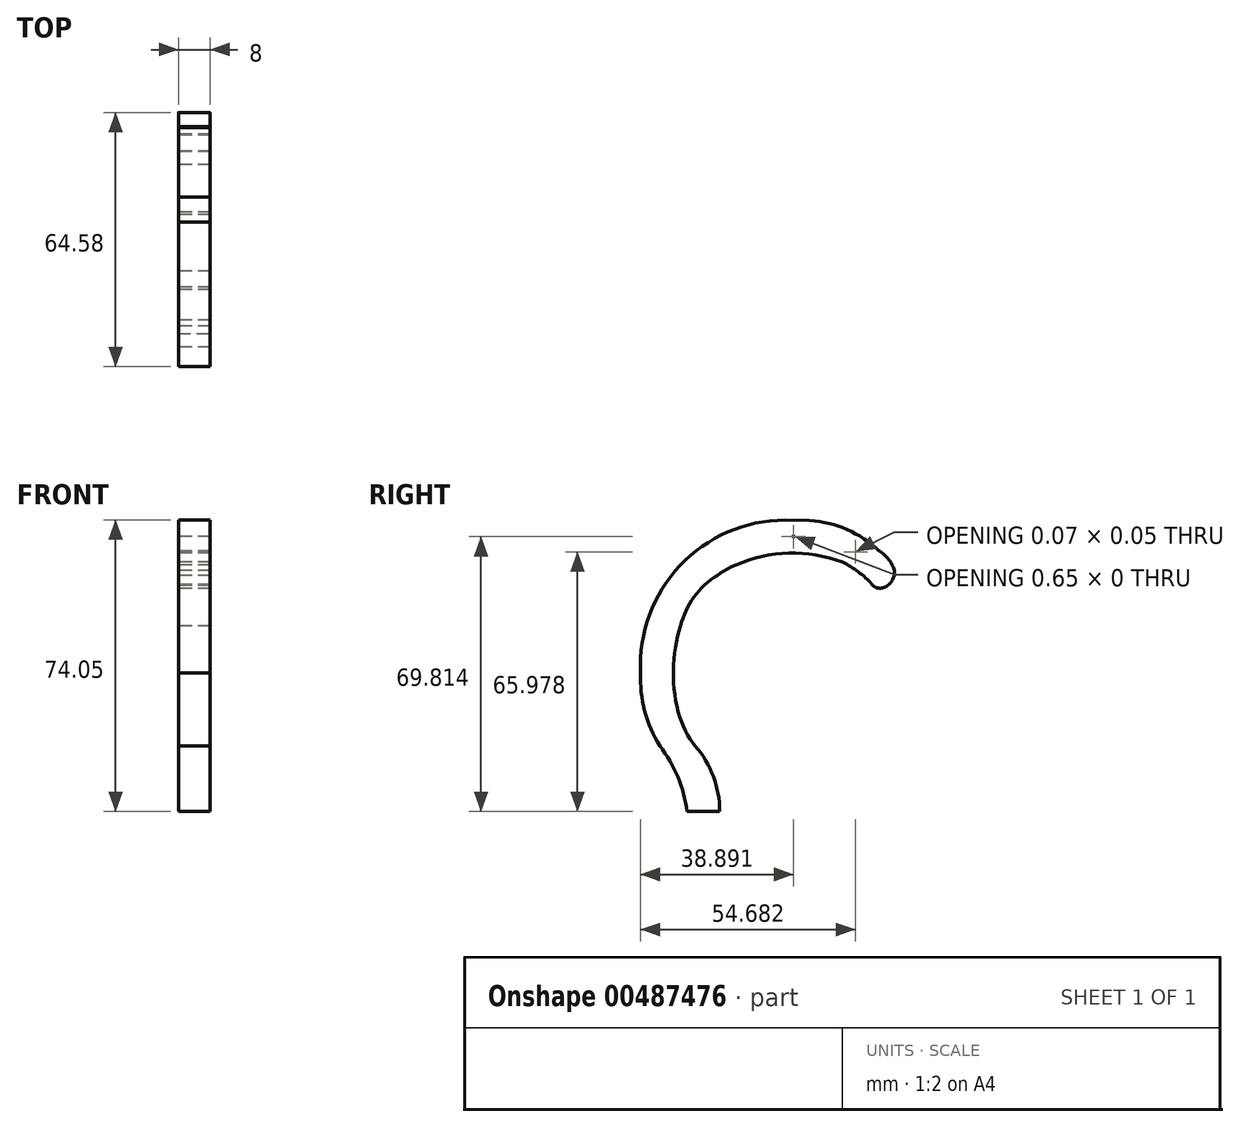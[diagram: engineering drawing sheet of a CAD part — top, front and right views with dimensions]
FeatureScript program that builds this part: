
annotation { "Feature Type Name" : "Feature", "Feature Type Description" : "" }
export const myFeature = defineFeature(function(context is Context, id is Id, definition is map)
    precondition{}
    {
        {
            var Q0;
            Q0=qCreatedBy(makeId("Right.planeOp"),FACE);
            var sketch = newSketch(context, id + "F0", { "sketchPlane" : qUnion([Q0])});
            skLineSegment(sketch, "E0", {"start": v(4.15, 0.16) * mm, "end": v(4.15, 6.8) * mm});
            skPoint(sketch, "E1.endSnap0", {"position": v(4.15, 42.04) * mm});
            skEllipticalArc(sketch, "E2", {});
            skPoint(sketch, "E3.visualSharp", {"position": v(4.15, 20.16) * mm});
            skArc(sketch, "E3.filletArc", {"start": v(4.15, 6.8) * mm, "mid": v(2.55, 15.7) * mm, "end": v(-2.07, 23.46) * mm});
            skArc(sketch, "E4", {"start": v(8.27, 69.42) * mm, "mid": v(5.83, 68.26) * mm, "end": v(3.55, 66.8) * mm});
            skArc(sketch, "E5", {"start": v(3.55, 66.8) * mm, "mid": v(-2.39, 61.28) * mm, "end": v(-5.75, 53.92) * mm});
            skArc(sketch, "E6", {"start": v(35.3, 70.17) * mm, "mid": v(21.71, 72.44) * mm, "end": v(8.27, 69.42) * mm});
            skArc(sketch, "E7", {"start": v(45.47, 63.6) * mm, "mid": v(47.84, 65.26) * mm, "end": v(48.55, 68.06) * mm});
            skPoint(sketch, "E8.startSnap0", {"position": v(21.71, 72.44) * mm});
            skLineSegment(sketch, "E9", {"start": v(42.86, 64.52) * mm, "end": v(43.11, 64.23) * mm});
            skLineSegment(sketch, "E10", {"start": v(-7.64, 42.04) * mm, "end": v(-15.95, 42.04) * mm});
            skPoint(sketch, "E10.endSnap0", {"position": v(-7.64, 42.04) * mm});
            skArc(sketch, "E11", {"start": v(22.57, 80.82) * mm, "mid": v(-5.28, 69.95) * mm, "end": v(-15.95, 42.04) * mm});
            skArc(sketch, "E12", {"start": v(44.65, 73.03) * mm, "mid": v(35.35, 78.9) * mm, "end": v(24.5, 80.78) * mm});
            skLineSegment(sketch, "E13", {"start": v(4.15, 6.8) * mm, "end": v(-4.16, 6.8) * mm});
            skLineSegment(sketch, "E14", {"start": v(-2.07, 23.46) * mm, "end": v(-11.07, 23.46) * mm});
            skArc(sketch, "E15", {"start": v(-15.95, 42.04) * mm, "mid": v(-14.9, 32.38) * mm, "end": v(-11.07, 23.46) * mm});
            skArc(sketch, "E16", {"start": v(-4.16, 6.8) * mm, "mid": v(-6.46, 15.6) * mm, "end": v(-11.07, 23.46) * mm});
            skLineSegment(sketch, "E17", {"start": v(20.65, 80.85) * mm, "end": v(27, 80.73) * mm});
            skPoint(sketch, "E8.start.orphan", {"position": v(23.7, 72.44) * mm});
            skArc(sketch, "E18", {"start": v(42.86, 64.52) * mm, "mid": v(44.03, 63.67) * mm, "end": v(45.47, 63.6) * mm});
            skArc(sketch, "E19", {"start": v(48.55, 68.06) * mm, "mid": v(47.05, 70.9) * mm, "end": v(44.65, 73.03) * mm});
            skArc(sketch, "E20", {"start": v(43.11, 64.23) * mm, "mid": v(39.5, 67.6) * mm, "end": v(35.3, 70.17) * mm});
            skLineSegment(sketch, "E21", {"start": v(-5.75, 53.92) * mm, "end": v(-14.63, 53.92) * mm});
            skLineSegment(sketch, "E22", {"start": v(3.55, 66.8) * mm, "end": v(-8.08, 66.8) * mm});
            skLineSegment(sketch, "E23", {"start": v(8.27, 69.42) * mm, "end": v(-5.8, 69.42) * mm});
            skLineSegment(sketch, "E24", {"start": v(-2.26, 72.67) * mm, "end": v(-2.26, 61.45) * mm});
            skPoint(sketch, "E24.startSnap0", {"position": v(-2.26, 66.8) * mm});
            skPoint(sketch, "E24.endSnap0", {"position": v(-2.26, 66.8) * mm});
            skLineSegment(sketch, "E25", {"start": v(1.24, 75.17) * mm, "end": v(1.24, 65.14) * mm});
            skPoint(sketch, "E25.startSnap0", {"position": v(1.24, 69.42) * mm});
            skLineSegment(sketch, "E26", {"start": v(10.14, 79.25) * mm, "end": v(10.14, 70.18) * mm});
            skPoint(sketch, "E26.startSnap0", {"position": v(10.14, 72.45) * mm});
            skLineSegment(sketch, "E27", {"start": v(0.53, 74.71) * mm, "end": v(17.17, 74.71) * mm});
            skPoint(sketch, "E27.startSnap0", {"position": v(10.14, 74.71) * mm});
            skLineSegment(sketch, "E28", {"start": v(22.57, 80.82) * mm, "end": v(22.57, 72.41) * mm});
            skLineSegment(sketch, "E29", {"start": v(2.88, 76.61) * mm, "end": v(39.99, 76.61) * mm});
            skPoint(sketch, "E29.startSnap0", {"position": v(22.57, 76.61) * mm});
            skLineSegment(sketch, "E30", {"start": v(31.33, 80.12) * mm, "end": v(31.33, 71.4) * mm});
            skLineSegment(sketch, "E31", {"start": v(23.64, 75.76) * mm, "end": v(41.3, 75.76) * mm});
            skPoint(sketch, "E31.startSnap0", {"position": v(31.33, 75.76) * mm});
            skLineSegment(sketch, "E32", {"start": v(38.64, 77.39) * mm, "end": v(38.64, 68.22) * mm});
            skLineSegment(sketch, "E33", {"start": v(45, 72.8) * mm, "end": v(25.42, 72.64) * mm});
            skPoint(sketch, "E33.startSnap0", {"position": v(38.64, 72.8) * mm});
            skLineSegment(sketch, "E34", {"start": v(40, 67.2) * mm, "end": v(48.56, 67.2) * mm});
            skLineSegment(sketch, "E35", {"start": v(44.28, 67.2) * mm, "end": v(44.28, 63.6) * mm});
            skLineSegment(sketch, "E36", {"start": v(48.26, 66.02) * mm, "end": v(41.38, 66.02) * mm});
            skLineSegment(sketch, "E37", {"start": v(44.86, 63.6) * mm, "end": v(44.86, 74.93) * mm});
            skLineSegment(sketch, "E38", {"start": v(-6.62, 33.15) * mm, "end": v(-15.1, 33.15) * mm});
            skLineSegment(sketch, "E39", {"start": v(-5.2, 28.72) * mm, "end": v(-13.7, 28.72) * mm});
            skLineSegment(sketch, "E40", {"start": v(-6.46, 15.6) * mm, "end": v(2.58, 15.6) * mm});
            skLineSegment(sketch, "E41", {"start": v(-8.65, 19.94) * mm, "end": v(0.49, 19.94) * mm});
            skFitSpline(sketch, "E42", {"points": [v(0, 6.8) * mm, v(-1.94, 15.6) * mm, v(-4.08, 19.94) * mm, v(-6.57, 23.46) * mm, v(-9.45, 28.72) * mm, v(-10.86, 33.15) * mm, v(-11.8, 42.04) * mm, v(-10.19, 53.92) * mm, v(-2.26, 66.8) * mm, v(1.24, 70.16) * mm, v(10.14, 74.71) * mm, v(22.57, 76.61) * mm, v(31.33, 75.76) * mm, v(38.64, 72.8) * mm, v(44.28, 67.2) * mm, v(44.86, 66.02) * mm], "startDerivative": vector(-23.04, 130.46) * mm, "endDerivative": vector(11.67, -34.63) * mm});
            const initialGuessF0  = {"E2": [0.004152898933041244, 0.04203729945250362, 0, -1, 0.021873103824685693, 0.011794387804632158, 4.1382491567360145, 5.727505896014558]};
            skSetInitialGuess(sketch, initialGuessF0);
            skSolve(sketch);
        }
        {
            var Q0;
            Q0=qCreatedBy(makeId("Front.planeOp"),FACE);
            var sketch = newSketch(context, id + "F1", { "sketchPlane" : qUnion([Q0])});
            skLineSegment(sketch, "E43", {"start": v(0, 0) * mm, "end": v(0, 6.8) * mm});
            skLineSegment(sketch, "E44", {"start": v(0, 6.8) * mm, "end": v(0, 19.94) * mm});
            skLineSegment(sketch, "E45", {"start": v(0, 19.94) * mm, "end": v(0, 69.14) * mm});
            skLineSegment(sketch, "E46", {"start": v(0, 44.54) * mm, "end": v(12.18, 44.54) * mm});
            skPoint(sketch, "E46.endSnap0", {"position": v(0, 44.54) * mm});
            skEllipse(sketch, "E47", {"center": v(0, 44.54) * mm, "majorRadius": 24.6 * mm, "minorRadius": 12.18 * mm, "majorAxis": v(0, 1)});
            skLineSegment(sketch, "E48", {"start": v(0, 37.35) * mm, "end": v(11.64, 37.35) * mm});
            skLineSegment(sketch, "E49", {"start": v(0, 30.71) * mm, "end": v(10.07, 30.71) * mm});
            skLineSegment(sketch, "E50", {"start": v(0, 26.9) * mm, "end": v(8.49, 26.9) * mm});
            skLineSegment(sketch, "E51", {"start": v(0, 41.38) * mm, "end": v(12.07, 41.38) * mm});
            skLineSegment(sketch, "E52", {"start": v(0, 49.29) * mm, "end": v(11.95, 49.29) * mm});
            skLineSegment(sketch, "E53", {"start": v(0, 55.2) * mm, "end": v(10.97, 55.2) * mm});
            skSolve(sketch);
        }
        {
            var Q0;
            {var subQ1=sQuery(id+"F0.wireOp",EDGE,"E19");var subQ6=sQuery(id+"F0.wireOp",EDGE,"E7");var subQ9=makeQuery(id+"F0.imprint","INTERSECT",VERTEX,{"derivedFrom":[subQ6,subQ1]});Q0=makeQuery(id+"F0.imprint","IMPRINT",FACE,{"disambiguationData":[TD([[makeQuery(id+"F0.imprint","IMPRINT",EDGE,{"disambiguationData":[TD([[subQ9,1.0]])],"derivedFrom":subQ6}),1.0]])]});}
            var Q1;
            {var subQ1=sQuery(id+"F0.wireOp",EDGE,"E7");var subQ5=sQuery(id+"F0.wireOp",EDGE,"E18");var subQ8=makeQuery(id+"F0.imprint","INTERSECT",VERTEX,{"derivedFrom":[subQ1,subQ5]});Q1=makeQuery(id+"F0.imprint","IMPRINT",FACE,{"disambiguationData":[TD([[makeQuery(id+"F0.imprint","IMPRINT",EDGE,{"disambiguationData":[TD([[subQ8,-1.0]])],"derivedFrom":subQ1}),1.0]])]});}
            var Q2;
            {var subQ0=sQuery(id+"F0.wireOp",EDGE,"E34");var subQ1=sQuery(id+"F0.wireOp",EDGE,"E7");var subQ2=makeQuery(id+"F0.imprint","INTERSECT",VERTEX,{"derivedFrom":[subQ1,subQ0]});Q2=makeQuery(id+"F0.imprint","IMPRINT",FACE,{"disambiguationData":[TD([[makeQuery(id+"F0.imprint","IMPRINT",EDGE,{"disambiguationData":[TD([[subQ2,1.0]])],"derivedFrom":subQ1}),1.0]])]});}
            var Q3;
            {var subQ0=sQuery(id+"F0.wireOp",EDGE,"E34");var subQ1=sQuery(id+"F0.wireOp",EDGE,"E20");var subQ2=makeQuery(id+"F0.imprint","INTERSECT",VERTEX,{"derivedFrom":[subQ1,subQ0]});Q3=makeQuery(id+"F0.imprint","IMPRINT",FACE,{"disambiguationData":[TD([[makeQuery(id+"F0.imprint","IMPRINT",EDGE,{"disambiguationData":[TD([[subQ2,1.0]])],"derivedFrom":subQ1}),-1.0]])]});}
            var Q4;
            {var subQ2=sQuery(id+"F0.wireOp",EDGE,"E9");Q4=makeQuery(id+"F0.imprint","IMPRINT",FACE,{"disambiguationData":[TD([[makeQuery(id+"F0.imprint","IMPRINT",EDGE,{"derivedFrom":subQ2}),1.0]])]});}
            var Q5;
            {var subQ1=sQuery(id+"F0.wireOp",EDGE,"E20");var subQ5=sQuery(id+"F0.wireOp",EDGE,"E32");var subQ6=makeQuery(id+"F0.imprint","INTERSECT",VERTEX,{"derivedFrom":[subQ1,subQ5]});Q5=makeQuery(id+"F0.imprint","IMPRINT",FACE,{"disambiguationData":[TD([[makeQuery(id+"F0.imprint","IMPRINT",EDGE,{"disambiguationData":[TD([[subQ6,1.0]])],"derivedFrom":subQ1}),-1.0]])]});}
            var Q6;
            {var subQ0=sQuery(id+"F0.wireOp",EDGE,"E37");var subQ1=sQuery(id+"F0.wireOp",EDGE,"E33");var subQ2=makeQuery(id+"F0.imprint","INTERSECT",VERTEX,{"derivedFrom":[subQ1,subQ0]});Q6=makeQuery(id+"F0.imprint","IMPRINT",FACE,{"disambiguationData":[TD([[makeQuery(id+"F0.imprint","IMPRINT",EDGE,{"disambiguationData":[TD([[subQ2,-1.0]])],"derivedFrom":subQ1}),1.0]])]});}
            var Q7;
            {var subQ5=sQuery(id+"F0.wireOp",EDGE,"E19");var subQ6=sQuery(id+"F0.wireOp",EDGE,"E12");var subQ7=makeQuery(id+"F0.imprint","INTERSECT",VERTEX,{"derivedFrom":[subQ6,subQ5]});Q7=makeQuery(id+"F0.imprint","IMPRINT",FACE,{"disambiguationData":[TD([[makeQuery(id+"F0.imprint","IMPRINT",EDGE,{"disambiguationData":[TD([[subQ7,-1.0]])],"derivedFrom":subQ6}),1.0]])]});}
            var Q8;
            {var subQ0=sQuery(id+"F0.wireOp",EDGE,"E29");var subQ1=sQuery(id+"F0.wireOp",EDGE,"E12");var subQ2=makeQuery(id+"F0.imprint","INTERSECT",VERTEX,{"derivedFrom":[subQ1,subQ0]});Q8=makeQuery(id+"F0.imprint","IMPRINT",FACE,{"disambiguationData":[TD([[makeQuery(id+"F0.imprint","IMPRINT",EDGE,{"disambiguationData":[TD([[subQ2,1.0]])],"derivedFrom":subQ1}),1.0]])]});}
            var Q9;
            {var subQ0=sQuery(id+"F0.wireOp",EDGE,"E29");var subQ1=sQuery(id+"F0.wireOp",EDGE,"E12");var subQ2=makeQuery(id+"F0.imprint","INTERSECT",VERTEX,{"derivedFrom":[subQ1,subQ0]});Q9=makeQuery(id+"F0.imprint","IMPRINT",FACE,{"disambiguationData":[TD([[makeQuery(id+"F0.imprint","IMPRINT",EDGE,{"disambiguationData":[TD([[subQ2,-1.0]])],"derivedFrom":subQ1}),1.0]])]});}
            var Q10;
            {var subQ0=sQuery(id+"F0.wireOp",EDGE,"E30");var subQ1=sQuery(id+"F0.wireOp",EDGE,"E29");var subQ2=makeQuery(id+"F0.imprint","INTERSECT",VERTEX,{"derivedFrom":[subQ1,subQ0]});Q10=makeQuery(id+"F0.imprint","IMPRINT",FACE,{"disambiguationData":[TD([[makeQuery(id+"F0.imprint","IMPRINT",EDGE,{"disambiguationData":[TD([[subQ2,-1.0]])],"derivedFrom":subQ1}),-1.0]])]});}
            var Q11;
            {var subQ0=sQuery(id+"F0.wireOp",EDGE,"E30");var subQ1=sQuery(id+"F0.wireOp",EDGE,"E12");var subQ2=makeQuery(id+"F0.imprint","INTERSECT",VERTEX,{"derivedFrom":[subQ1,subQ0]});Q11=makeQuery(id+"F0.imprint","IMPRINT",FACE,{"disambiguationData":[TD([[makeQuery(id+"F0.imprint","IMPRINT",EDGE,{"disambiguationData":[TD([[subQ2,1.0]])],"derivedFrom":subQ1}),1.0]])]});}
            var Q12;
            {var subQ0=sQuery(id+"F0.wireOp",EDGE,"E32");var subQ1=sQuery(id+"F0.wireOp",EDGE,"E31");var subQ2=makeQuery(id+"F0.imprint","INTERSECT",VERTEX,{"derivedFrom":[subQ1,subQ0]});Q12=makeQuery(id+"F0.imprint","IMPRINT",FACE,{"disambiguationData":[TD([[makeQuery(id+"F0.imprint","IMPRINT",EDGE,{"disambiguationData":[TD([[subQ2,-1.0]])],"derivedFrom":subQ0}),-1.0]])]});}
            var Q13;
            {var subQ3=sQuery(id+"F0.wireOp",EDGE,"E42");var subQ5=sQuery(id+"F0.wireOp",EDGE,"E32");var subQ6=makeQuery(id+"F0.imprint","INTERSECT",VERTEX,{"derivedFrom":[subQ5,subQ3]});Q13=makeQuery(id+"F0.imprint","IMPRINT",FACE,{"disambiguationData":[TD([[makeQuery(id+"F0.imprint","IMPRINT",EDGE,{"disambiguationData":[TD([[subQ6,-1.0]])],"derivedFrom":subQ5}),-1.0]])]});}
            var Q14;
            {var subQ1=sQuery(id+"F0.wireOp",EDGE,"E20");var subQ6=sQuery(id+"F0.wireOp",EDGE,"E6");var subQ9=makeQuery(id+"F0.imprint","INTERSECT",VERTEX,{"derivedFrom":[subQ6,subQ1]});Q14=makeQuery(id+"F0.imprint","IMPRINT",FACE,{"disambiguationData":[TD([[makeQuery(id+"F0.imprint","IMPRINT",EDGE,{"disambiguationData":[TD([[subQ9,-1.0]])],"derivedFrom":subQ6}),-1.0]])]});}
            var Q15;
            {var subQ1=sQuery(id+"F0.wireOp",EDGE,"E17");var subQ6=sQuery(id+"F0.wireOp",EDGE,"E12");var subQ8=makeQuery(id+"F0.imprint","INTERSECT",VERTEX,{"disambiguationData":[OD(1.0)],"derivedFrom":[subQ6,subQ1]});Q15=makeQuery(id+"F0.imprint","IMPRINT",FACE,{"disambiguationData":[TD([[makeQuery(id+"F0.imprint","IMPRINT",EDGE,{"disambiguationData":[TD([[subQ8,1.0]])],"derivedFrom":subQ6}),1.0]])]});}
            var Q16;
            {var subQ0=sQuery(id+"F0.wireOp",EDGE,"E30");var subQ8=sQuery(id+"F0.wireOp",EDGE,"E6");var subQ10=makeQuery(id+"F0.imprint","INTERSECT",VERTEX,{"derivedFrom":[subQ8,subQ0]});Q16=makeQuery(id+"F0.imprint","IMPRINT",FACE,{"disambiguationData":[TD([[makeQuery(id+"F0.imprint","IMPRINT",EDGE,{"disambiguationData":[TD([[subQ10,-1.0]])],"derivedFrom":subQ8}),-1.0]])]});}
            var Q17;
            {var subQ0=sQuery(id+"F0.wireOp",EDGE,"E42");var subQ1=sQuery(id+"F0.wireOp",EDGE,"E29");var subQ2=makeQuery(id+"F0.imprint","INTERSECT",VERTEX,{"derivedFrom":[subQ1,subQ0]});Q17=makeQuery(id+"F0.imprint","IMPRINT",FACE,{"disambiguationData":[TD([[makeQuery(id+"F0.imprint","IMPRINT",EDGE,{"disambiguationData":[TD([[subQ2,-1.0]])],"derivedFrom":subQ1}),-1.0]])]});}
            var Q18;
            {var subQ1=sQuery(id+"F0.wireOp",EDGE,"E35");var subQ3=sQuery(id+"F0.wireOp",EDGE,"E36");var subQ4=makeQuery(id+"F0.imprint","INTERSECT",VERTEX,{"derivedFrom":[subQ1,subQ3]});Q18=makeQuery(id+"F0.imprint","IMPRINT",FACE,{"disambiguationData":[TD([[makeQuery(id+"F0.imprint","IMPRINT",EDGE,{"disambiguationData":[TD([[subQ4,1.0]])],"derivedFrom":subQ1}),1.0]])]});}
            var Q19;
            {var subQ1=sQuery(id+"F0.wireOp",EDGE,"E34");var subQ3=sQuery(id+"F0.wireOp",EDGE,"E37");var subQ4=makeQuery(id+"F0.imprint","INTERSECT",VERTEX,{"derivedFrom":[subQ1,subQ3]});Q19=makeQuery(id+"F0.imprint","IMPRINT",FACE,{"disambiguationData":[TD([[makeQuery(id+"F0.imprint","IMPRINT",EDGE,{"disambiguationData":[TD([[subQ4,1.0]])],"derivedFrom":subQ1}),-1.0]])]});}
            var Q20;
            {var subQ1=sQuery(id+"F0.wireOp",EDGE,"E17");var subQ2=sQuery(id+"F0.wireOp",EDGE,"E11");var subQ9=makeQuery(id+"F0.imprint","INTERSECT",VERTEX,{"derivedFrom":[subQ2,subQ1]});Q20=makeQuery(id+"F0.imprint","IMPRINT",FACE,{"disambiguationData":[TD([[makeQuery(id+"F0.imprint","IMPRINT",EDGE,{"disambiguationData":[TD([[subQ9,-1.0]])],"derivedFrom":subQ2}),1.0]])]});}
            var Q21;
            {var subQ0=sQuery(id+"F0.wireOp",EDGE,"E29");var subQ1=sQuery(id+"F0.wireOp",EDGE,"E26");var subQ2=makeQuery(id+"F0.imprint","INTERSECT",VERTEX,{"derivedFrom":[subQ1,subQ0]});Q21=makeQuery(id+"F0.imprint","IMPRINT",FACE,{"disambiguationData":[TD([[makeQuery(id+"F0.imprint","IMPRINT",EDGE,{"disambiguationData":[TD([[subQ2,-1.0]])],"derivedFrom":subQ1}),1.0]])]});}
            var Q22;
            {var subQ0=sQuery(id+"F0.wireOp",EDGE,"E26");var subQ1=sQuery(id+"F0.wireOp",EDGE,"E6");var subQ2=makeQuery(id+"F0.imprint","INTERSECT",VERTEX,{"derivedFrom":[subQ1,subQ0]});Q22=makeQuery(id+"F0.imprint","IMPRINT",FACE,{"disambiguationData":[TD([[makeQuery(id+"F0.imprint","IMPRINT",EDGE,{"disambiguationData":[TD([[subQ2,1.0]])],"derivedFrom":subQ1}),-1.0]])]});}
            var Q23;
            {var subQ0=sQuery(id+"F0.wireOp",EDGE,"E26");var subQ1=sQuery(id+"F0.wireOp",EDGE,"E11");var subQ2=makeQuery(id+"F0.imprint","INTERSECT",VERTEX,{"derivedFrom":[subQ1,subQ0]});Q23=makeQuery(id+"F0.imprint","IMPRINT",FACE,{"disambiguationData":[TD([[makeQuery(id+"F0.imprint","IMPRINT",EDGE,{"disambiguationData":[TD([[subQ2,-1.0]])],"derivedFrom":subQ1}),1.0]])]});}
            var Q24;
            {var subQ1=sQuery(id+"F0.wireOp",EDGE,"E25");var subQ7=sQuery(id+"F0.wireOp",EDGE,"E11");var subQ8=makeQuery(id+"F0.imprint","INTERSECT",VERTEX,{"derivedFrom":[subQ7,subQ1]});Q24=makeQuery(id+"F0.imprint","IMPRINT",FACE,{"disambiguationData":[TD([[makeQuery(id+"F0.imprint","IMPRINT",EDGE,{"disambiguationData":[TD([[subQ8,1.0]])],"derivedFrom":subQ7}),1.0]])]});}
            var Q25;
            {var subQ0=sQuery(id+"F0.wireOp",EDGE,"E27");var subQ1=sQuery(id+"F0.wireOp",EDGE,"E25");var subQ2=makeQuery(id+"F0.imprint","INTERSECT",VERTEX,{"derivedFrom":[subQ1,subQ0]});Q25=makeQuery(id+"F0.imprint","IMPRINT",FACE,{"disambiguationData":[TD([[makeQuery(id+"F0.imprint","IMPRINT",EDGE,{"disambiguationData":[TD([[subQ2,-1.0]])],"derivedFrom":subQ1}),1.0]])]});}
            var Q26;
            {var subQ5=sQuery(id+"F0.wireOp",EDGE,"E25");var subQ7=sQuery(id+"F0.wireOp",EDGE,"E23");var subQ8=makeQuery(id+"F0.imprint","INTERSECT",VERTEX,{"derivedFrom":[subQ7,subQ5]});Q26=makeQuery(id+"F0.imprint","IMPRINT",FACE,{"disambiguationData":[TD([[makeQuery(id+"F0.imprint","IMPRINT",EDGE,{"disambiguationData":[TD([[subQ8,1.0]])],"derivedFrom":subQ5}),1.0]])]});}
            var Q27;
            {var subQ0=sQuery(id+"F0.wireOp",EDGE,"E4");Q27=makeQuery(id+"F0.imprint","IMPRINT",FACE,{"disambiguationData":[TD([[makeQuery(id+"F0.imprint","IMPRINT",EDGE,{"derivedFrom":subQ0}),-1.0]])]});}
            var Q28;
            {var subQ7=sQuery(id+"F0.wireOp",EDGE,"E24");var subQ9=sQuery(id+"F0.wireOp",EDGE,"E11");var subQ10=makeQuery(id+"F0.imprint","INTERSECT",VERTEX,{"derivedFrom":[subQ9,subQ7]});Q28=makeQuery(id+"F0.imprint","IMPRINT",FACE,{"disambiguationData":[TD([[makeQuery(id+"F0.imprint","IMPRINT",EDGE,{"disambiguationData":[TD([[subQ10,1.0]])],"derivedFrom":subQ9}),1.0]])]});}
            var Q29;
            {var subQ0=sQuery(id+"F0.wireOp",EDGE,"E42");var subQ1=sQuery(id+"F0.wireOp",EDGE,"E23");var subQ2=makeQuery(id+"F0.imprint","INTERSECT",VERTEX,{"derivedFrom":[subQ1,subQ0]});Q29=makeQuery(id+"F0.imprint","IMPRINT",FACE,{"disambiguationData":[TD([[makeQuery(id+"F0.imprint","IMPRINT",EDGE,{"disambiguationData":[TD([[subQ2,-1.0]])],"derivedFrom":subQ1}),1.0]])]});}
            var Q30;
            {var subQ0=sQuery(id+"F0.wireOp",EDGE,"E25");var subQ5=sQuery(id+"F0.wireOp",EDGE,"E23");var subQ6=makeQuery(id+"F0.imprint","INTERSECT",VERTEX,{"derivedFrom":[subQ5,subQ0]});Q30=makeQuery(id+"F0.imprint","IMPRINT",FACE,{"disambiguationData":[TD([[makeQuery(id+"F0.imprint","IMPRINT",EDGE,{"disambiguationData":[TD([[subQ6,-1.0]])],"derivedFrom":subQ5}),1.0]])]});}
            var Q31;
            {var subQ1=sQuery(id+"F0.wireOp",EDGE,"E5");var subQ3=sQuery(id+"F0.wireOp",EDGE,"E25");var subQ4=makeQuery(id+"F0.imprint","INTERSECT",VERTEX,{"derivedFrom":[subQ1,subQ3]});Q31=makeQuery(id+"F0.imprint","IMPRINT",FACE,{"disambiguationData":[TD([[makeQuery(id+"F0.imprint","IMPRINT",EDGE,{"disambiguationData":[TD([[subQ4,1.0]])],"derivedFrom":subQ3}),1.0]])]});}
            var Q32;
            {var subQ0=sQuery(id+"F0.wireOp",EDGE,"E24");var subQ1=sQuery(id+"F0.wireOp",EDGE,"E5");var subQ2=makeQuery(id+"F0.imprint","INTERSECT",VERTEX,{"derivedFrom":[subQ1,subQ0]});Q32=makeQuery(id+"F0.imprint","IMPRINT",FACE,{"disambiguationData":[TD([[makeQuery(id+"F0.imprint","IMPRINT",EDGE,{"disambiguationData":[TD([[subQ2,1.0]])],"derivedFrom":subQ1}),-1.0]])]});}
            var Q33;
            {var subQ1=sQuery(id+"F0.wireOp",EDGE,"E5");var subQ3=sQuery(id+"F0.wireOp",EDGE,"E24");var subQ4=makeQuery(id+"F0.imprint","INTERSECT",VERTEX,{"derivedFrom":[subQ1,subQ3]});Q33=makeQuery(id+"F0.imprint","IMPRINT",FACE,{"disambiguationData":[TD([[makeQuery(id+"F0.imprint","IMPRINT",EDGE,{"disambiguationData":[TD([[subQ4,-1.0]])],"derivedFrom":subQ1}),-1.0]])]});}
            var Q34;
            {var subQ0=sQuery(id+"F0.wireOp",EDGE,"E21");var subQ1=sQuery(id+"F0.wireOp",EDGE,"E11");var subQ2=makeQuery(id+"F0.imprint","INTERSECT",VERTEX,{"derivedFrom":[subQ1,subQ0]});Q34=makeQuery(id+"F0.imprint","IMPRINT",FACE,{"disambiguationData":[TD([[makeQuery(id+"F0.imprint","IMPRINT",EDGE,{"disambiguationData":[TD([[subQ2,1.0]])],"derivedFrom":subQ1}),1.0]])]});}
            var Q35;
            {var subQ0=sQuery(id+"F0.wireOp",EDGE,"E22");var subQ1=sQuery(id+"F0.wireOp",EDGE,"E11");var subQ2=makeQuery(id+"F0.imprint","INTERSECT",VERTEX,{"derivedFrom":[subQ1,subQ0]});Q35=makeQuery(id+"F0.imprint","IMPRINT",FACE,{"disambiguationData":[TD([[makeQuery(id+"F0.imprint","IMPRINT",EDGE,{"disambiguationData":[TD([[subQ2,1.0]])],"derivedFrom":subQ1}),1.0]])]});}
            var Q36;
            {var subQ0=sQuery(id+"F0.wireOp",EDGE,"E23");var subQ1=sQuery(id+"F0.wireOp",EDGE,"E11");var subQ2=makeQuery(id+"F0.imprint","INTERSECT",VERTEX,{"derivedFrom":[subQ1,subQ0]});Q36=makeQuery(id+"F0.imprint","IMPRINT",FACE,{"disambiguationData":[TD([[makeQuery(id+"F0.imprint","IMPRINT",EDGE,{"disambiguationData":[TD([[subQ2,1.0]])],"derivedFrom":subQ1}),1.0]])]});}
            var Q37;
            {var subQ0=sQuery(id+"F0.wireOp",EDGE,"E25");var subQ1=sQuery(id+"F0.wireOp",EDGE,"E23");var subQ2=makeQuery(id+"F0.imprint","INTERSECT",VERTEX,{"derivedFrom":[subQ1,subQ0]});Q37=makeQuery(id+"F0.imprint","IMPRINT",FACE,{"disambiguationData":[TD([[makeQuery(id+"F0.imprint","IMPRINT",EDGE,{"disambiguationData":[TD([[subQ2,-1.0]])],"derivedFrom":subQ1}),-1.0]])]});}
            var Q38;
            {var subQ0=sQuery(id+"F0.wireOp",EDGE,"E25");var subQ1=sQuery(id+"F0.wireOp",EDGE,"E11");var subQ2=makeQuery(id+"F0.imprint","INTERSECT",VERTEX,{"derivedFrom":[subQ1,subQ0]});Q38=makeQuery(id+"F0.imprint","IMPRINT",FACE,{"disambiguationData":[TD([[makeQuery(id+"F0.imprint","IMPRINT",EDGE,{"disambiguationData":[TD([[subQ2,-1.0]])],"derivedFrom":subQ1}),1.0]])]});}
            var Q39;
            {var subQ1=sQuery(id+"F0.wireOp",EDGE,"E2");var subQ3=sQuery(id+"F0.wireOp",EDGE,"E10");var subQ4=makeQuery(id+"F0.imprint","INTERSECT",VERTEX,{"derivedFrom":[subQ1,subQ3]});Q39=makeQuery(id+"F0.imprint","IMPRINT",FACE,{"disambiguationData":[TD([[makeQuery(id+"F0.imprint","IMPRINT",EDGE,{"disambiguationData":[TD([[subQ4,-1.0]])],"derivedFrom":subQ3}),-1.0]])]});}
            var Q40;
            {var subQ0=sQuery(id+"F0.wireOp",EDGE,"E11");var subQ5=sQuery(id+"F0.wireOp",EDGE,"E21");var subQ6=makeQuery(id+"F0.imprint","INTERSECT",VERTEX,{"derivedFrom":[subQ0,subQ5]});Q40=makeQuery(id+"F0.imprint","IMPRINT",FACE,{"disambiguationData":[TD([[makeQuery(id+"F0.imprint","IMPRINT",EDGE,{"disambiguationData":[TD([[subQ6,1.0]])],"derivedFrom":subQ5}),1.0]])]});}
            var Q41;
            {var subQ0=sQuery(id+"F0.wireOp",EDGE,"E15");var subQ5=sQuery(id+"F0.wireOp",EDGE,"E38");var subQ6=makeQuery(id+"F0.imprint","INTERSECT",VERTEX,{"derivedFrom":[subQ0,subQ5]});Q41=makeQuery(id+"F0.imprint","IMPRINT",FACE,{"disambiguationData":[TD([[makeQuery(id+"F0.imprint","IMPRINT",EDGE,{"disambiguationData":[TD([[subQ6,1.0]])],"derivedFrom":subQ5}),-1.0]])]});}
            var Q42;
            {var subQ0=sQuery(id+"F0.wireOp",EDGE,"E10");var subQ1=sQuery(id+"F0.wireOp",EDGE,"E2");var subQ2=makeQuery(id+"F0.imprint","INTERSECT",VERTEX,{"derivedFrom":[subQ1,subQ0]});Q42=makeQuery(id+"F0.imprint","IMPRINT",FACE,{"disambiguationData":[TD([[makeQuery(id+"F0.imprint","IMPRINT",EDGE,{"disambiguationData":[TD([[subQ2,-1.0]])],"derivedFrom":subQ1}),-1.0]])]});}
            var Q43;
            {var subQ0=sQuery(id+"F0.wireOp",EDGE,"E38");var subQ1=sQuery(id+"F0.wireOp",EDGE,"E2");var subQ2=makeQuery(id+"F0.imprint","INTERSECT",VERTEX,{"derivedFrom":[subQ1,subQ0]});Q43=makeQuery(id+"F0.imprint","IMPRINT",FACE,{"disambiguationData":[TD([[makeQuery(id+"F0.imprint","IMPRINT",EDGE,{"disambiguationData":[TD([[subQ2,-1.0]])],"derivedFrom":subQ1}),-1.0]])]});}
            var Q44;
            {var subQ0=sQuery(id+"F0.wireOp",EDGE,"E38");var subQ1=sQuery(id+"F0.wireOp",EDGE,"E15");var subQ2=makeQuery(id+"F0.imprint","INTERSECT",VERTEX,{"derivedFrom":[subQ1,subQ0]});Q44=makeQuery(id+"F0.imprint","IMPRINT",FACE,{"disambiguationData":[TD([[makeQuery(id+"F0.imprint","IMPRINT",EDGE,{"disambiguationData":[TD([[subQ2,-1.0]])],"derivedFrom":subQ1}),1.0]])]});}
            var Q45;
            {var subQ0=sQuery(id+"F0.wireOp",EDGE,"E15");var subQ5=sQuery(id+"F0.wireOp",EDGE,"E39");var subQ6=makeQuery(id+"F0.imprint","INTERSECT",VERTEX,{"derivedFrom":[subQ0,subQ5]});Q45=makeQuery(id+"F0.imprint","IMPRINT",FACE,{"disambiguationData":[TD([[makeQuery(id+"F0.imprint","IMPRINT",EDGE,{"disambiguationData":[TD([[subQ6,1.0]])],"derivedFrom":subQ5}),1.0]])]});}
            var Q46;
            {var subQ1=sQuery(id+"F0.wireOp",EDGE,"E2");var subQ3=sQuery(id+"F0.wireOp",EDGE,"E39");var subQ4=makeQuery(id+"F0.imprint","INTERSECT",VERTEX,{"derivedFrom":[subQ1,subQ3]});Q46=makeQuery(id+"F0.imprint","IMPRINT",FACE,{"disambiguationData":[TD([[makeQuery(id+"F0.imprint","IMPRINT",EDGE,{"disambiguationData":[TD([[subQ4,-1.0]])],"derivedFrom":subQ3}),1.0]])]});}
            var Q47;
            {var subQ1=sQuery(id+"F0.wireOp",EDGE,"E3.filletArc");var subQ3=sQuery(id+"F0.wireOp",EDGE,"E41");var subQ4=makeQuery(id+"F0.imprint","INTERSECT",VERTEX,{"derivedFrom":[subQ1,subQ3]});Q47=makeQuery(id+"F0.imprint","IMPRINT",FACE,{"disambiguationData":[TD([[makeQuery(id+"F0.imprint","IMPRINT",EDGE,{"disambiguationData":[TD([[subQ4,1.0]])],"derivedFrom":subQ3}),1.0]])]});}
            var Q48;
            {var subQ0=sQuery(id+"F0.wireOp",EDGE,"E16");var subQ5=sQuery(id+"F0.wireOp",EDGE,"E41");var subQ6=makeQuery(id+"F0.imprint","INTERSECT",VERTEX,{"derivedFrom":[subQ0,subQ5]});Q48=makeQuery(id+"F0.imprint","IMPRINT",FACE,{"disambiguationData":[TD([[makeQuery(id+"F0.imprint","IMPRINT",EDGE,{"disambiguationData":[TD([[subQ6,-1.0]])],"derivedFrom":subQ5}),1.0]])]});}
            var Q49;
            {var subQ0=sQuery(id+"F0.wireOp",EDGE,"E40");var subQ1=sQuery(id+"F0.wireOp",EDGE,"E16");var subQ2=makeQuery(id+"F0.imprint","INTERSECT",VERTEX,{"derivedFrom":[subQ1,subQ0]});Q49=makeQuery(id+"F0.imprint","IMPRINT",FACE,{"disambiguationData":[TD([[makeQuery(id+"F0.imprint","IMPRINT",EDGE,{"disambiguationData":[TD([[subQ2,-1.0]])],"derivedFrom":subQ1}),-1.0]])]});}
            var Q50;
            {var subQ0=sQuery(id+"F0.wireOp",EDGE,"E40");var subQ1=sQuery(id+"F0.wireOp",EDGE,"E3.filletArc");var subQ2=makeQuery(id+"F0.imprint","INTERSECT",VERTEX,{"derivedFrom":[subQ1,subQ0]});Q50=makeQuery(id+"F0.imprint","IMPRINT",FACE,{"disambiguationData":[TD([[makeQuery(id+"F0.imprint","IMPRINT",EDGE,{"disambiguationData":[TD([[subQ2,-1.0]])],"derivedFrom":subQ1}),1.0]])]});}
            var Q51;
            {var subQ0=sQuery(id+"F0.wireOp",EDGE,"E16");var subQ1=sQuery(id+"F0.wireOp",EDGE,"E13");var subQ2=makeQuery(id+"F0.imprint","INTERSECT",VERTEX,{"derivedFrom":[subQ1,subQ0]});Q51=makeQuery(id+"F0.imprint","IMPRINT",FACE,{"disambiguationData":[TD([[makeQuery(id+"F0.imprint","IMPRINT",EDGE,{"disambiguationData":[TD([[subQ2,1.0]])],"derivedFrom":subQ1}),-1.0]])]});}
            var Q52;
            {var subQ0=sQuery(id+"F0.wireOp",EDGE,"E13");var subQ1=sQuery(id+"F0.wireOp",EDGE,"E3.filletArc");var subQ2=makeQuery(id+"F0.imprint","INTERSECT",VERTEX,{"derivedFrom":[subQ1,subQ0]});Q52=makeQuery(id+"F0.imprint","IMPRINT",FACE,{"disambiguationData":[TD([[makeQuery(id+"F0.imprint","IMPRINT",EDGE,{"disambiguationData":[TD([[subQ2,-1.0]])],"derivedFrom":subQ1}),1.0]])]});}
            extrude(context, id + "F2", {"entities" : qUnion([Q0, Q1, Q2, Q3, Q4, Q5, Q6, Q7, Q8, Q9, Q10, Q11, Q12, Q13, Q14, Q15, Q16, Q17, Q18, Q19, Q20, Q21, Q22, Q23, Q24, Q25, Q26, Q27, Q28, Q29, Q30, Q31, Q32, Q33, Q34, Q35, Q36, Q37, Q38, Q39, Q40, Q41, Q42, Q43, Q44, Q45, Q46, Q47, Q48, Q49, Q50, Q51, Q52]), "depth" : 8 * mm, "offsetDistance" : 25.4 * mm});
        }
    });
